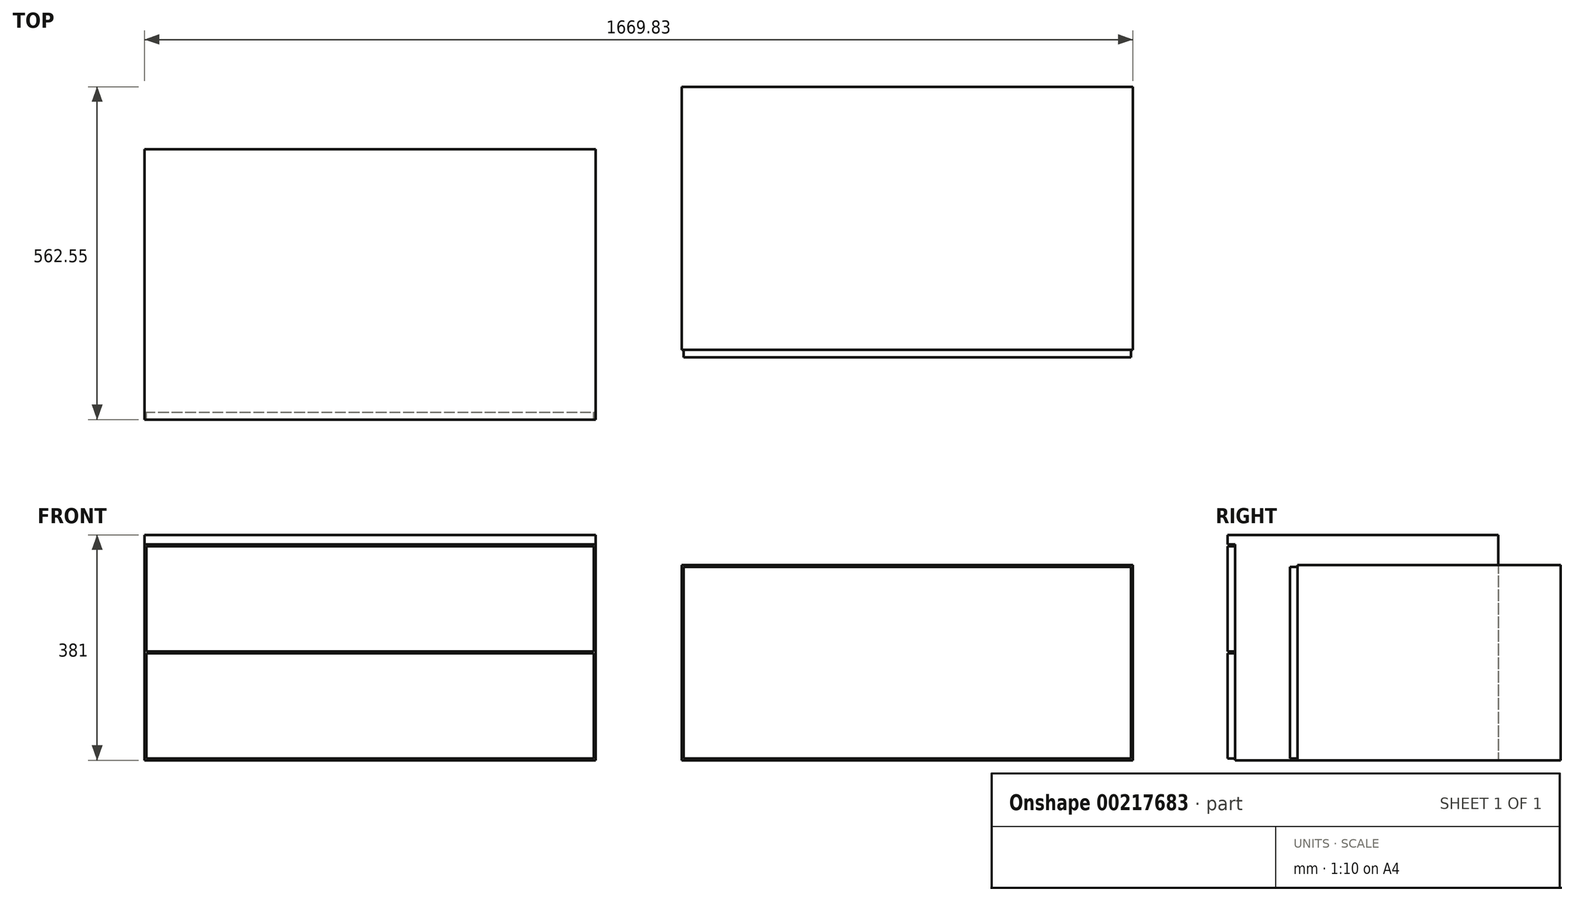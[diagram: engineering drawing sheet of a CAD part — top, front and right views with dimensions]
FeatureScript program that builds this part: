
annotation { "Feature Type Name" : "Feature", "Feature Type Description" : "" }
export const myFeature = defineFeature(function(context is Context, id is Id, definition is map)
    precondition{}
    {
        {
            var Q0;
            Q0=qCreatedBy(makeId("Top.planeOp"),FACE);
            var sketch = newSketch(context, id + "F0", { "sketchPlane" : qUnion([Q0])});
            skLineSegment(sketch, "E0.bottom", {"start": v(-659.6, 220.02) * mm, "end": v(102.4, 220.02) * mm});
            skLineSegment(sketch, "E0.top", {"start": v(-659.6, -224.48) * mm, "end": v(102.4, -224.48) * mm});
            skLineSegment(sketch, "E0.left", {"start": v(-659.6, 220.02) * mm, "end": v(-659.6, -224.48) * mm});
            skLineSegment(sketch, "E0.right", {"start": v(102.4, 220.02) * mm, "end": v(102.4, -224.48) * mm});
            skSolve(sketch);
        }
        {
            var Q0;
            Q0=qSketchRegion(id+"F0",true);
            extrude(context, id + "F1", {"entities" : qUnion([Q0]), "depth" : 381 * mm});
        }
        {
            var Q0;
            Q0=makeQuery(id+"F1.opExtrude","SWEPT_FACE",FACE,{"disambiguationData":[OSD([sQuery(id+"F0.wireOp",EDGE,"E0.top")])]});
            var sketch = newSketch(context, id + "F2", { "sketchPlane" : qUnion([Q0])});
            skLineSegment(sketch, "E1.bottom", {"start": v(-656.42, 180.98) * mm, "end": v(99.23, 180.98) * mm});
            skLineSegment(sketch, "E1.top", {"start": v(-656.42, 3.17) * mm, "end": v(99.23, 3.17) * mm});
            skLineSegment(sketch, "E1.left", {"start": v(-656.42, 180.98) * mm, "end": v(-656.42, 3.17) * mm});
            skLineSegment(sketch, "E1.right", {"start": v(99.23, 180.98) * mm, "end": v(99.23, 3.18) * mm});
            skLineSegment(sketch, "E2.bottom", {"start": v(-656.42, 361.95) * mm, "end": v(99.23, 361.95) * mm});
            skLineSegment(sketch, "E2.top", {"start": v(-656.42, 184.15) * mm, "end": v(99.23, 184.15) * mm});
            skLineSegment(sketch, "E2.left", {"start": v(-656.42, 361.95) * mm, "end": v(-656.42, 184.15) * mm});
            skLineSegment(sketch, "E2.right", {"start": v(99.23, 361.95) * mm, "end": v(99.23, 184.15) * mm});
            skLineSegment(sketch, "E3.bottom", {"start": v(-659.6, 381) * mm, "end": v(102.4, 381) * mm});
            skLineSegment(sketch, "E3.top", {"start": v(-659.6, 365.13) * mm, "end": v(102.4, 365.13) * mm});
            skLineSegment(sketch, "E3.left", {"start": v(-659.6, 381) * mm, "end": v(-659.6, 365.13) * mm});
            skLineSegment(sketch, "E3.right", {"start": v(102.4, 381) * mm, "end": v(102.4, 365.13) * mm});
            skSolve(sketch);
        }
        {
            var Q0;
            Q0=makeQuery(id+"F2.imprint","IMPRINT",FACE,{"disambiguationData":[TD([[makeQuery(id+"F2.imprint","IMPRINT",EDGE,{"derivedFrom":sQuery(id+"F2.wireOp",EDGE,"E1.bottom")}),-1.0]])]});
            var Q1;
            Q1=makeQuery(id+"F2.imprint","IMPRINT",FACE,{"disambiguationData":[TD([[makeQuery(id+"F2.imprint","IMPRINT",EDGE,{"derivedFrom":sQuery(id+"F2.wireOp",EDGE,"E2.bottom")}),-1.0]])]});
            var Q2;
            Q2=makeQuery(id+"F2.imprint","IMPRINT",FACE,{"disambiguationData":[TD([[makeQuery(id+"F2.imprint","IMPRINT",EDGE,{"derivedFrom":sQuery(id+"F2.wireOp",EDGE,"E3.bottom")}),-1.0]])]});
            extrude(context, id + "F3", {"entities" : qUnion([Q0, Q1, Q2]), "operationType" : NewBodyOperationType.ADD, "depth" : 12.7 * mm});
        }
        {
            var Q0;
            Q0=qCreatedBy(makeId("Top.planeOp"),FACE);
            var sketch = newSketch(context, id + "F4", { "sketchPlane" : qUnion([Q0])});
            skLineSegment(sketch, "E4.bottom", {"start": v(248.23, 325.37) * mm, "end": v(1010.23, 325.37) * mm});
            skLineSegment(sketch, "E4.top", {"start": v(248.23, -119.13) * mm, "end": v(1010.23, -119.13) * mm});
            skLineSegment(sketch, "E4.left", {"start": v(248.23, 325.37) * mm, "end": v(248.23, -119.13) * mm});
            skLineSegment(sketch, "E4.right", {"start": v(1010.23, 325.37) * mm, "end": v(1010.23, -119.13) * mm});
            skSolve(sketch);
        }
        {
            var Q0;
            Q0=makeQuery(id+"F4.imprint","IMPRINT",FACE,{"disambiguationData":[TD([[makeQuery(id+"F4.imprint","IMPRINT",EDGE,{"derivedFrom":sQuery(id+"F4.wireOp",EDGE,"E4.bottom")}),-1.0]])]});
            extrude(context, id + "F5", {"entities" : qUnion([Q0]), "depth" : 330.2 * mm});
        }
        {
            var Q0;
            Q0=makeQuery(id+"F5.opExtrude","SWEPT_FACE",FACE,{"disambiguationData":[OSD([sQuery(id+"F4.wireOp",EDGE,"E4.top")])]});
            var sketch = newSketch(context, id + "F6", { "sketchPlane" : qUnion([Q0])});
            skLineSegment(sketch, "E5.bottom", {"start": v(251.4, 327.03) * mm, "end": v(1007.06, 327.03) * mm});
            skLineSegment(sketch, "E5.top", {"start": v(251.4, 3.18) * mm, "end": v(1007.06, 3.18) * mm});
            skLineSegment(sketch, "E5.left", {"start": v(251.4, 327.03) * mm, "end": v(251.4, 3.18) * mm});
            skLineSegment(sketch, "E5.right", {"start": v(1007.06, 327.03) * mm, "end": v(1007.06, 3.18) * mm});
            skSolve(sketch);
        }
        {
            var Q0;
            Q0=qSketchRegion(id+"F6",true);
            extrude(context, id + "F7", {"entities" : qUnion([Q0]), "operationType" : NewBodyOperationType.ADD, "depth" : 12.7 * mm});
        }
    });
